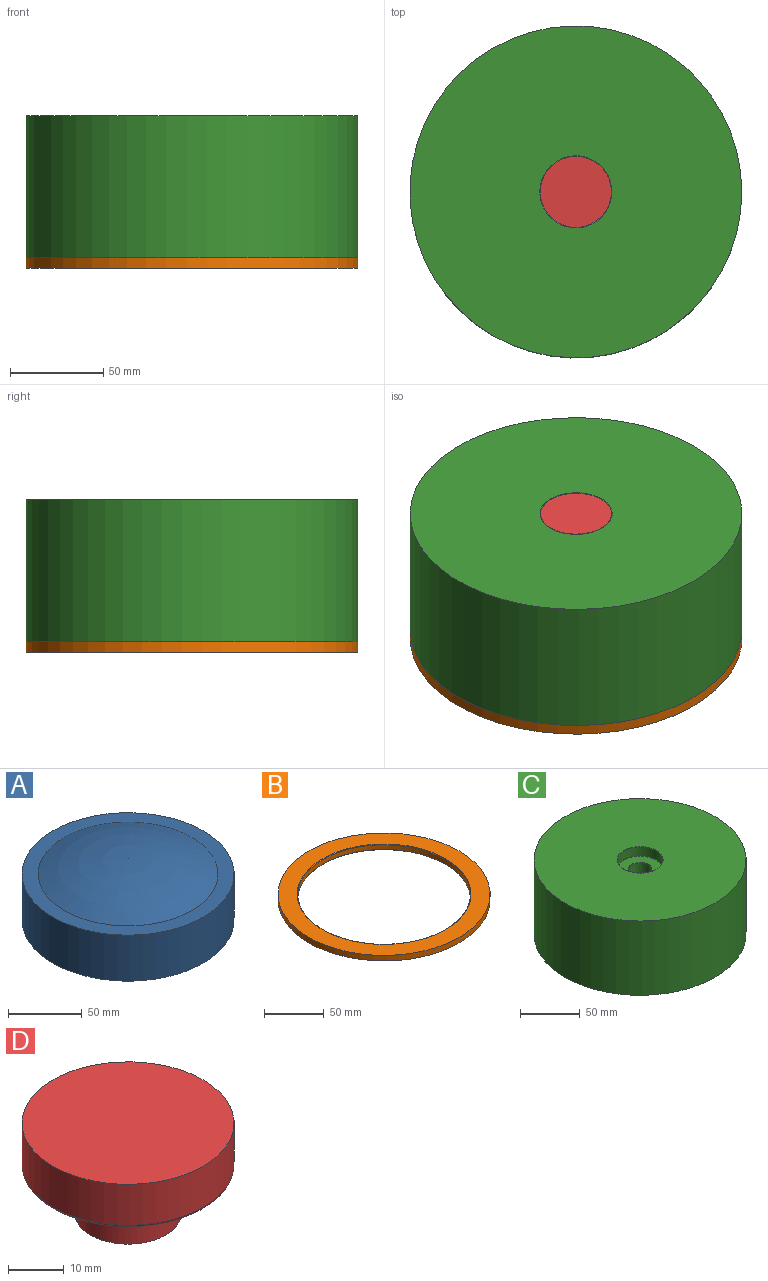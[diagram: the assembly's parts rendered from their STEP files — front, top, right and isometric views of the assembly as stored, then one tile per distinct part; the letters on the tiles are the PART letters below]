
ASSEMBLY  parts=4 mates=3
PART A: 4 faces, bbox 143.5x143.5x50.9 mm
  f0: cylinder r=71.75mm len=143.51mm, axis (0,0,-1), area 17177.4mm2, adj f1,f2
  f1: plane 143.51x143.51mm, normal (0,0,1), area 4549.4mm2, adj f0,f3
  f2: plane 143.51x143.51mm, normal (0,0,-1), area 16175.4mm2, adj f0
  f3: torus R=1.57mm, axis (0,0,-1), area 12159.5mm2, adj f1
PART B: 6 faces, bbox 177.8x177.8x5.7 mm
  f0: cylinder r=72.39mm len=144.78mm, axis (0,0,1), area 2114.2mm2, adj f4,f5
  f1: cylinder r=88.9mm len=177.8mm, axis (0,0,1), area 3163.9mm2, adj f2,f3
  f2: plane 177.8x177.8mm, normal (0,0,-1), area 8133.9mm2, adj f1,f5
  f3: plane 177.8x177.8mm, normal (0,0,1), area 8133.9mm2, adj f1,f4
  f4: torus R=72.9mm, axis (0,0,1), area 363.9mm2, adj f0,f3
  f5: torus R=72.9mm, axis (0,0,1), area 363.9mm2, adj f0,f2
PART C: 13 faces, bbox 177.8x177.8x76.2 mm
  f0: cylinder r=9.53mm len=19.05mm, axis (0,0,1), area 605.1mm2, adj f5,f10
  f1: cylinder r=88.9mm len=177.8mm, axis (0,0,-1), area 42563.4mm2, adj f2,f3
  f2: plane 177.8x177.8mm, normal (0,0,1), area 23658mm2, adj f1,f11
  f3: plane 177.8x177.8mm, normal (0,0,-1), area 8423.5mm2, adj f1,f9
  f4: cylinder r=71.75mm len=143.51mm, axis (0,0,-1), area 17830.1mm2, adj f6,f9
  f5: torus R=3.6mm, axis (0,0,1), area 16090.8mm2, adj f0,f6
  f6: plane 143.51x143.51mm, normal (0,0,-1), area 702.2mm2, adj f4,f5
  f7: plane 37.59x37.59mm, normal (0,0,1), area 809.5mm2, adj f10,f12
  f8: cylinder r=19.05mm len=38.1mm, axis (0,0,1), area 1079.3mm2, adj f11,f12
  f9: torus R=72.26mm, axis (0,0,1), area 360.7mm2, adj f3,f4
  f10: torus R=9.78mm, axis (0,0,1), area 24.1mm2, adj f0,f7
  f11: torus R=19.3mm, axis (0,0,1), area 48mm2, adj f2,f8
  f12: torus R=18.8mm, axis (0,0,1), area 47.5mm2, adj f7,f8
PART D: 7 faces, bbox 41.2x41.2x19.9 mm
  f0: cylinder r=19.05mm len=38.1mm, axis (0,0,-1), area 1079.3mm2, adj f1,f6
  f1: plane 38.1x38.1mm, normal (0,0,1), area 1140.1mm2, adj f0
  f2: plane 37.08x37.08mm, normal (0,0,-1), area 763.9mm2, adj f5,f6
  f3: cylinder r=9.53mm len=19.05mm, axis (0,0,1), area 589.8mm2, adj f4,f5
  f4: plane 19.05x19.05mm, normal (0,0,-1), area 285mm2, adj f3
  f5: torus R=10.03mm, axis (0,0,1), area 48.7mm2, adj f2,f3
  f6: torus R=18.54mm, axis (0,0,1), area 94.6mm2, adj f0,f2
PLACE A t=(-3.92,65.6,1.83)mm
PLACE B rot(axis=(1,0,0),180deg) t=(-3.92,65.6,1.83)mm
PLACE C t=(-3.92,65.6,7.5)mm
PLACE D t=(-3.92,65.6,74.17)mm
MATE fastened A.f0 <-> C.f5  axis (0,0,1) through (-3.92,65.6,39.93)mm
MATE fastened B.f1 <-> C.f1  axis (0,0,1) through (-3.92,65.6,7.5)mm
MATE fastened C.f8 <-> D.f0  axis (0,0,1) through (-3.92,65.6,74.17)mm
